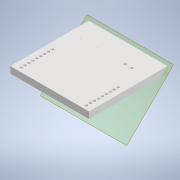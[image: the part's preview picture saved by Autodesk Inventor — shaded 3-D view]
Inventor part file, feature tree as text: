
AUTODESK INVENTOR PART (.ipt)
format: ipt  version: 2021.2 (Build 252289000, 289)  size: 157,184 bytes
history: native  units: mm
features: sketch x4, hole x3, other x2, extrude x1
ambient origin geometry x8: Origin, YZ Plane, XZ Plane, XY Plane, X Axis, Y Axis, Z Axis, Center Point
bodies: Body1 (feature_tree)
feature tree (10):
  other  "Твердое тело1"
  extrude  "Выдавливание1"  Depth=5.0mm TaperAngle=0.0deg
  sketch  "Эскиз2"
  hole  "Отверстие1"  [1 undecoded]
  hole  "Отверстие2"  [1 undecoded]
  hole  "Отверстие3"  [1 undecoded]
  other  "РабПлоскость1"
  sketch  "Эскиз1"
  sketch  "Эскиз3"
  sketch  "Эскиз4"
note: 3 required parameter values undecoded (feature->parameter linkage not recoverable at this tier; creation-order binding heuristic only, values carry confidence <= 0.55)
